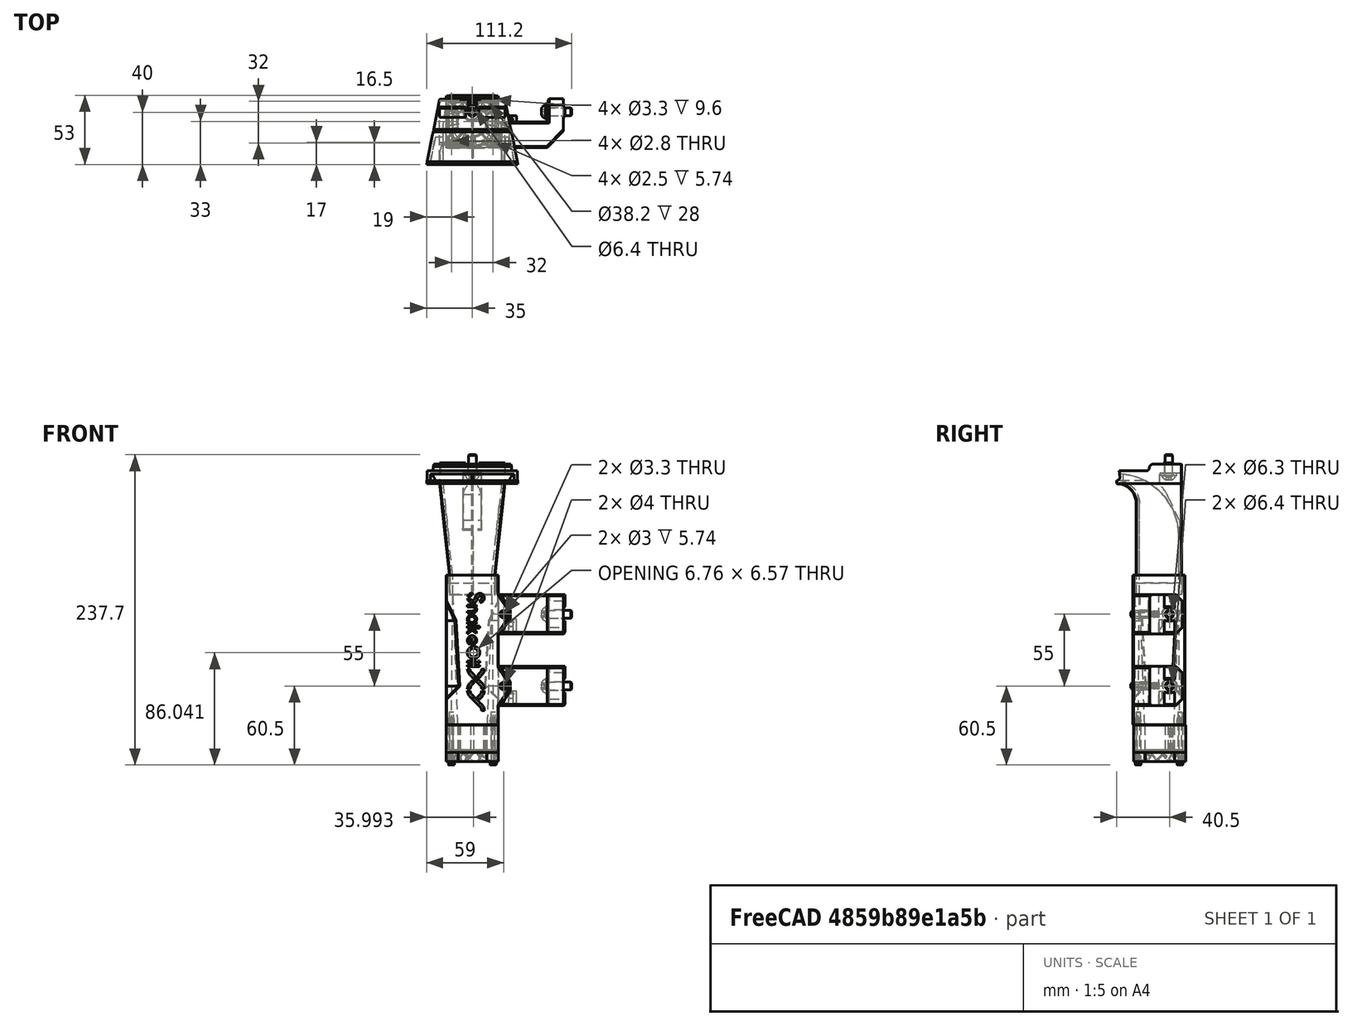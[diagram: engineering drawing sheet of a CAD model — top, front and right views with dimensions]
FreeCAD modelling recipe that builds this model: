
FCSTD DOCUMENT  (FreeCAD 0.19R24291 (Git))
Label: side-blower-4028-assembly
License: All rights reserved
LicenseURL: http://en.wikipedia.org/wiki/All_rights_reserved
objects: Part::FeaturePython×18, Part::Feature×5, PartDesign::CoordinateSystem×1, App::Part×1
note: 24 computed .brp shape members not serialized (recipe doc carries the construction recipe); baked Part::Feature solids carry a one-line shape summary decoded from their .brp

FEATURE [Part::Feature] Body003001  label="180-duct-angled"
  shape: bbox 70.02 x 51.77 x 101 mm, 88 faces (baked)
FEATURE [Part::Feature] Cut001  label="fan-mounter"
  shape: bbox 48 x 40 x 115 mm, 3175 faces, 2 solids (baked)
FEATURE [Part::Feature] Body009001  label="mounter-arm"
  Placement = pos=(20,0.5,-30) rot=(0,0,1;0rad)
  shape: bbox 50.85 x 37.5 x 30 mm, 59 faces (baked)
FEATURE [Part::Feature] Body009002  label="mounter-arm001"
  Placement = pos=(20,0.5,-85) rot=(0,0,1;0rad)
  shape: bbox 50.85 x 37.5 x 30 mm, 59 faces (baked)
FEATURE [Part::FeaturePython] HeatSet  label="M3-HeatSet"  # WARN: FeaturePython — macro-defined, semantics opaque (R4)
  Placement = pos=(24,-17.5,-70) rot=(-1,0,0;1.5708rad)
  baseObject = -> Body009002 [Edge2]
  diameter = 3
  invert = true
  leftHanded = false
  offset = 0
FEATURE [Part::FeaturePython] HeatSet001  label="M3-HeatSet001"  # WARN: FeaturePython — macro-defined, semantics opaque (R4)
  Placement = pos=(24,-17.5,-15) rot=(-1,0,0;1.5708rad)
  baseObject = -> Body009001 [Edge2]
  diameter = 3
  invert = true
  leftHanded = false
  offset = 0
FEATURE [Part::FeaturePython] HeatSet002  label="M2.5-HeatSet"  # WARN: FeaturePython — macro-defined, semantics opaque (R4)
  Placement = pos=(16,-33.5,-100) rot=(-1,0,0;3.14159rad)
  baseObject = -> Cut001 [Edge2491]
  diameter = 2
  invert = false
  leftHanded = false
  offset = 0
FEATURE [Part::FeaturePython] HeatSet003  label="M2.5-HeatSet001"  # WARN: FeaturePython — macro-defined, semantics opaque (R4)
  Placement = pos=(-16,-33.5,-100) rot=(-1,0,0;3.14159rad)
  baseObject = -> Cut001 [Edge2494]
  diameter = 2
  invert = false
  leftHanded = false
  offset = 0
FEATURE [Part::FeaturePython] HeatSet004  label="M2.5-HeatSet002"  # WARN: FeaturePython — macro-defined, semantics opaque (R4)
  Placement = pos=(-16,-1.5,-100) rot=(-1,0,0;3.14159rad)
  baseObject = -> Cut001 [Edge2493]
  diameter = 2
  invert = false
  leftHanded = false
  offset = 0
FEATURE [Part::FeaturePython] HeatSet005  label="M2.5-HeatSet003"  # WARN: FeaturePython — macro-defined, semantics opaque (R4)
  Placement = pos=(16,-1.5,-100) rot=(-1,0,0;3.14159rad)
  baseObject = -> Cut001 [Edge2492]
  diameter = 2
  invert = false
  leftHanded = false
  offset = 0
FEATURE [Part::FeaturePython] Washer  label="M6-Washer"  # Fasteners workbench fastener (typed FeaturePython)
  Placement = pos=(58,-9.5,-15) rot=(0,-1,0;1.5708rad)
  baseObject = -> Body009001 [Edge6]
  diameter = 7
  invert = true
  leftHanded = false
  matchOuter = false
  offset = 0
  type = 3
FEATURE [Part::FeaturePython] Washer001  label="M6-Washer001"  # Fasteners workbench fastener (typed FeaturePython)
  Placement = pos=(58,-9.5,-70) rot=(0,-1,0;1.5708rad)
  baseObject = -> Body009002 [Edge6]
  diameter = 7
  invert = true
  leftHanded = false
  matchOuter = false
  offset = 0
  type = 3
FEATURE [Part::FeaturePython] Screw  label="M6x20-Screw"  # Fasteners workbench fastener (typed FeaturePython)
  Placement = pos=(56.2,-9.5,-15) rot=(0,-1,0;1.5708rad)
  baseObject = -> Washer [Edge1]
  diameter = 4
  invert = false
  leftHanded = false
  length = 4
  lengthCustom = 20
  matchOuter = false
  offset = 0
  thread = false
  type = 42
FEATURE [Part::FeaturePython] Screw001  label="M6x20-Screw001"  # Fasteners workbench fastener (typed FeaturePython)
  Placement = pos=(56.2,-9.5,-70) rot=(0,-1,0;1.5708rad)
  baseObject = -> Washer001 [Edge1]
  diameter = 4
  invert = false
  leftHanded = false
  length = 4
  lengthCustom = 20
  matchOuter = false
  offset = 0
  thread = false
  type = 42
FEATURE [Part::FeaturePython] Washer002  label="M6-Washer002"  # Fasteners workbench fastener (typed FeaturePython)
  Placement = pos=(0,-10,93) rot=(-1,0,0;3.14159rad)
  baseObject = -> Body003001 [Edge127]
  diameter = 7
  invert = true
  leftHanded = false
  matchOuter = false
  offset = 0
  type = 3
FEATURE [Part::FeaturePython] Screw002  label="M6x16-Screw"  # Fasteners workbench fastener (typed FeaturePython)
  Placement = pos=(0,-10,91.2) rot=(-1,0,0;3.14159rad)
  baseObject = -> Washer002 [Edge1]
  diameter = 4
  invert = false
  leftHanded = false
  length = 3
  lengthCustom = 16
  matchOuter = false
  offset = 0
  thread = false
  type = 42
FEATURE [Part::FeaturePython] Screw003  label="M3x20-Screw"  # Fasteners workbench fastener (typed FeaturePython)
  Placement = pos=(24,-37.5,-15) rot=(1,0,0;1.5708rad)
  baseObject = -> Cut001 [Edge106]
  diameter = 1
  invert = false
  leftHanded = false
  length = 6
  lengthCustom = 20
  matchOuter = false
  offset = 0
  thread = false
  type = 42
FEATURE [Part::FeaturePython] Screw004  label="M3x20-Screw001"  # Fasteners workbench fastener (typed FeaturePython)
  Placement = pos=(24,-37.5,-70) rot=(1,0,0;1.5708rad)
  baseObject = -> Cut001 [Edge1423]
  diameter = 1
  invert = false
  leftHanded = false
  length = 6
  lengthCustom = 20
  matchOuter = false
  offset = 0
  thread = false
  type = 42
FEATURE [Part::FeaturePython] Screw005  label="M2.5x30-Screw"  # Fasteners workbench fastener (typed FeaturePython)
  Placement = pos=(16,-1.5,-128) rot=(-1,0,0;3.14159rad)
  baseObject = -> HeatSet005 [Edge1]
  diameter = 3
  invert = false
  leftHanded = false
  length = 10
  lengthCustom = 30
  matchOuter = false
  offset = 28
  thread = false
  type = 36
FEATURE [Part::FeaturePython] Screw006  label="M2.5x30-Screw001"  # Fasteners workbench fastener (typed FeaturePython)
  Placement = pos=(-16,-1.5,-128) rot=(-1,0,0;3.14159rad)
  baseObject = -> HeatSet004 [Edge1]
  diameter = 3
  invert = false
  leftHanded = false
  length = 10
  lengthCustom = 30
  matchOuter = false
  offset = 28
  thread = false
  type = 36
FEATURE [Part::FeaturePython] Screw007  label="M2.5x30-Screw002"  # Fasteners workbench fastener (typed FeaturePython)
  Placement = pos=(-16,-33.5,-128) rot=(-1,0,0;3.14159rad)
  baseObject = -> HeatSet003 [Edge1]
  diameter = 3
  invert = false
  leftHanded = false
  length = 10
  lengthCustom = 30
  matchOuter = false
  offset = 28
  thread = false
  type = 36
FEATURE [Part::FeaturePython] Screw008  label="M2.5x30-Screw003"  # Fasteners workbench fastener (typed FeaturePython)
  Placement = pos=(16,-33.5,-128) rot=(-1,0,0;3.14159rad)
  baseObject = -> HeatSet002 [Edge1]
  diameter = 3
  invert = false
  leftHanded = false
  length = 10
  lengthCustom = 30
  matchOuter = false
  offset = 28
  thread = false
  type = 36
FEATURE [Part::Feature] Body009003  label="4028-fan"
  Placement = pos=(0,-17,-118) rot=(1,0,0;1.5708rad)
  shape: bbox 40 x 40 x 28 mm, 104 faces (baked)
FEATURE [PartDesign::CoordinateSystem] LCS_aux_fan
  AttacherType = Attacher::AttachEngine3D
FEATURE [App::Part] Part  label="aux-fan"
  Group = -> [Body003001,Cut001,Body009001,Body009002,HeatSet,HeatSet001,HeatSet002,HeatSet003,HeatSet004,HeatSet005,Washer,Washer001,Screw,Screw001,Washer002,Screw002,Screw003,Screw004,Screw005,Screw006,Screw007,Screw008,Body009003,LCS_aux_fan]
  Origin = -> Origin
